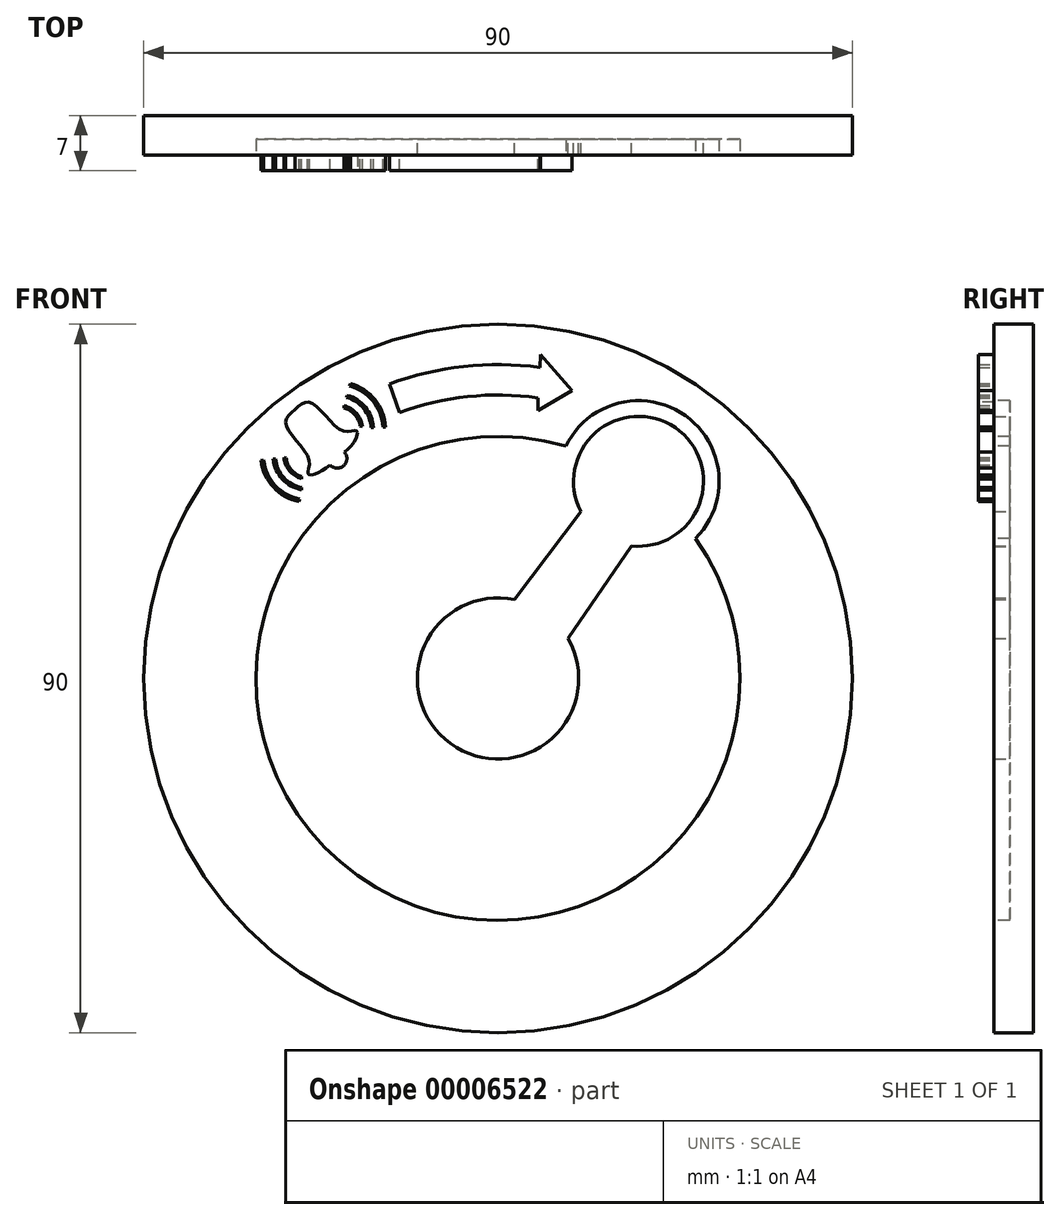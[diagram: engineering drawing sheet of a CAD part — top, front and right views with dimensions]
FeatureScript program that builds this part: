
annotation { "Feature Type Name" : "Feature", "Feature Type Description" : "" }
export const myFeature = defineFeature(function(context is Context, id is Id, definition is map)
    precondition{}
    {
        {
            var Q0;
            Q0=qCreatedBy(makeId("Front.planeOp"),FACE);
            var sketch = newSketch(context, id + "F0", { "sketchPlane" : qUnion([Q0])});
            skCircle(sketch, "E0", {"center": v(0, 0) * mm, "radius": 45 * mm});
            skSolve(sketch);
        }
        {
            var Q0;
            Q0=makeQuery(id+"F0.imprint","IMPRINT",FACE,{"disambiguationData":[TD([[makeQuery(id+"F0.imprint","IMPRINT",EDGE,{"derivedFrom":sQuery(id+"F0.wireOp",EDGE,"E0")}),1.0]])]});
            extrude(context, id + "F1", {"entities" : qUnion([Q0]), "depth" : 5 * mm});
        }
        {
            var Q0;
            Q0=makeQuery(id+"F1.opExtrude","CAP_FACE",FACE,{"disambiguationData":[OSD([sQuery(id+"F0.wireOp",EDGE,"E0")])],"isStart":false});
            var sketch = newSketch(context, id + "F2", { "sketchPlane" : qUnion([Q0])});
            skCircle(sketch, "E1", {"center": v(0, 0) * mm, "radius": 30.75 * mm});
            skCircle(sketch, "E2", {"center": v(17.84, 25.04) * mm, "radius": 10.25 * mm});
            skSolve(sketch);
        }
        {
            var Q0;
            {var subQ0=sQuery(id+"F2.wireOp",EDGE,"E2");var subQ1=sQuery(id+"F2.wireOp",EDGE,"E1");var subQ3=makeQuery(id+"F2.imprint","INTERSECT",VERTEX,{"disambiguationData":[OD(0.0)],"derivedFrom":[subQ1,subQ0]});var subQ5=makeQuery(id+"F2.imprint","IMPRINT",EDGE,{"disambiguationData":[TD([[subQ3,1.0]])],"derivedFrom":subQ1});Q0=qUnion([makeQuery(id+"F2.imprint","IMPRINT",FACE,{"disambiguationData":[TD([[subQ5,1.0]])]}),makeQuery(id+"F2.imprint","IMPRINT",FACE,{"disambiguationData":[TD([[subQ5,-1.0]])]}),makeQuery(id+"F2.imprint","IMPRINT",FACE,{"disambiguationData":[TD([[makeQuery(id+"F2.imprint","IMPRINT",EDGE,{"disambiguationData":[TD([[subQ3,-1.0]])],"derivedFrom":subQ1}),1.0]])]})]);}
            extrude(context, id + "F3", {"entities" : qUnion([Q0]), "operationType" : NewBodyOperationType.REMOVE, "oppositeDirection" : true, "depth" : 2 * mm});
        }
        {
            var Q0;
            Q0=makeQuery(id+"F3.boolean.opBoolean","COPY",FACE,{"derivedFrom":makeQuery(id+"F3.opExtrude","CAP_FACE",FACE,{"disambiguationData":[OSD([sQuery(id+"F2.wireOp",EDGE,"E1"),sQuery(id+"F2.wireOp",EDGE,"E2")])],"isStart":false})});
            var sketch = newSketch(context, id + "F4", { "sketchPlane" : qUnion([Q0])});
            skCircle(sketch, "E3", {"center": v(17.84, 25.04) * mm, "radius": 8.25 * mm});
            skSolve(sketch);
        }
        {
            var Q0;
            Q0=makeQuery(id+"F4.imprint","IMPRINT",FACE,{"disambiguationData":[TD([[makeQuery(id+"F4.imprint","IMPRINT",EDGE,{"derivedFrom":sQuery(id+"F4.wireOp",EDGE,"E3")}),1.0]])]});
            extrude(context, id + "F5", {"entities" : qUnion([Q0]), "operationType" : NewBodyOperationType.ADD, "depth" : 2 * mm});
        }
        {
            var Q0;
            Q0=makeQuery(id+"F3.boolean.opBoolean","COPY",FACE,{"derivedFrom":makeQuery(id+"F3.opExtrude","CAP_FACE",FACE,{"disambiguationData":[OSD([sQuery(id+"F2.wireOp",EDGE,"E1"),sQuery(id+"F2.wireOp",EDGE,"E2")])],"isStart":false})});
            var sketch = newSketch(context, id + "F6", { "sketchPlane" : qUnion([Q0])});
            skCircle(sketch, "E4", {"center": v(0, 0) * mm, "radius": 10.24 * mm});
            skLineSegment(sketch, "E5", {"start": v(2.1, 10.02) * mm, "end": v(10.52, 21.22) * mm});
            skLineSegment(sketch, "E6", {"start": v(8.9, 5.07) * mm, "end": v(16.92, 16.84) * mm});
            skLineSegment(sketch, "E7", {"start": v(10.52, 21.22) * mm, "end": v(16.92, 16.84) * mm});
            skSolve(sketch);
        }
        {
            var Q0;
            {var subQ0=sQuery(id+"F6.wireOp",EDGE,"E4");var subQ3=sQuery(id+"F6.wireOp",EDGE,"E5");var subQ4=makeQuery(id+"F6.imprint","INTERSECT",VERTEX,{"derivedFrom":[subQ0,subQ3]});var subQ5=makeQuery(id+"F6.imprint","IMPRINT",EDGE,{"disambiguationData":[TD([[subQ4,1.0]])],"derivedFrom":subQ0});var subQ7=sQuery(id+"F6.wireOp",EDGE,"E7");Q0=qUnion([makeQuery(id+"F6.imprint","IMPRINT",FACE,{"disambiguationData":[TD([[subQ5,1.0]])]}),makeQuery(id+"F6.imprint","IMPRINT",FACE,{"disambiguationData":[TD([[makeQuery(id+"F6.imprint","IMPRINT",EDGE,{"derivedFrom":subQ3}),-1.0]])]}),makeQuery(id+"F6.imprint","IMPRINT",FACE,{"disambiguationData":[TD([[makeQuery(id+"F6.imprint","IMPRINT",EDGE,{"derivedFrom":subQ7}),-1.0]])]})]);}
            extrude(context, id + "F7", {"entities" : qUnion([Q0]), "operationType" : NewBodyOperationType.ADD, "depth" : 2 * mm});
        }
        {
            var Q0;
            Q0=makeQuery(id+"F1.opExtrude","CAP_FACE",FACE,{"disambiguationData":[OSD([sQuery(id+"F0.wireOp",EDGE,"E0")])],"isStart":false});
            var sketch = newSketch(context, id + "F8", { "sketchPlane" : qUnion([Q0])});
            skArc(sketch, "E8", {"start": v(5.05, 35.65) * mm, "mid": v(-3.85, 35.8) * mm, "end": v(-12.5, 33.76) * mm});
            skArc(sketch, "E9", {"start": v(5.3, 39.5) * mm, "mid": v(-4.37, 39.63) * mm, "end": v(-13.78, 37.41) * mm});
            skLineSegment(sketch, "E10", {"start": v(-13.78, 37.41) * mm, "end": v(-12.5, 33.76) * mm});
            skLineSegment(sketch, "E11", {"start": v(5.05, 35.65) * mm, "end": v(5.05, 34.04) * mm});
            skLineSegment(sketch, "E12", {"start": v(5.05, 34.04) * mm, "end": v(9.4, 36.59) * mm});
            skLineSegment(sketch, "E13", {"start": v(9.4, 36.59) * mm, "end": v(5.39, 41.11) * mm});
            skLineSegment(sketch, "E14", {"start": v(5.39, 41.11) * mm, "end": v(5.3, 39.5) * mm});
            skLineSegment(sketch, "E15", {"start": v(-13.78, 37.41) * mm, "end": v(-13.44, 36.43) * mm});
            skSolve(sketch);
        }
        {
            var Q0;
            Q0=makeQuery(id+"F8.imprint","IMPRINT",FACE,{"disambiguationData":[TD([[makeQuery(id+"F8.imprint","IMPRINT",EDGE,{"derivedFrom":sQuery(id+"F8.wireOp",EDGE,"E8")}),-1.0]])]});
            extrude(context, id + "F9", {"entities" : qUnion([Q0]), "operationType" : NewBodyOperationType.ADD, "depth" : 2 * mm});
        }
        {
            var Q0;
            Q0=makeQuery(id+"F1.opExtrude","CAP_FACE",FACE,{"disambiguationData":[OSD([sQuery(id+"F0.wireOp",EDGE,"E0")])],"isStart":false});
            var sketch = newSketch(context, id + "F10", { "sketchPlane" : qUnion([Q0])});
            skFitSpline(sketch, "E16", {"points": [v(-25.8, 34.15) * mm, v(-23.73, 35) * mm, v(-19.68, 31.43) * mm, v(-17.99, 31.46) * mm, v(-18.08, 30.4) * mm, v(-20.44, 27.94) * mm], "startDerivative": vector(10.59, 9.7) * mm, "endDerivative": vector(-12.74, -9.93) * mm});
            skFitSpline(sketch, "E17.0.MirrorCS", {"points": [v(-25.8, 34.15) * mm, v(-26.94, 32.23) * mm, v(-24, 27.7) * mm, v(-24.15, 26.02) * mm, v(-23.2, 25.97) * mm, v(-20.44, 27.94) * mm], "startDerivative": vector(-11.14, -9.06) * mm, "endDerivative": vector(11.68, 11.16) * mm});
            skCircle(sketch, "E18", {"center": v(-20.44, 27.94) * mm, "radius": 1.24 * mm});
            skArc(sketch, "E19", {"start": v(-25.14, 34.76) * mm, "mid": v(-26.4, 34.85) * mm, "end": v(-26.5, 33.59) * mm});
            skSolve(sketch);
        }
        {
            var Q0;
            Q0 = qSketchRegion(id + "F10", true);
            extrude(context, id + "F11", {"entities" : qUnion([Q0]), "operationType" : NewBodyOperationType.ADD, "depth" : 2 * mm});
        }
        {
            var Q0;
            Q0=makeQuery(id+"F1.opExtrude","CAP_FACE",FACE,{"disambiguationData":[OSD([sQuery(id+"F0.wireOp",EDGE,"E0")])],"isStart":false});
            var sketch = newSketch(context, id + "F12", { "sketchPlane" : qUnion([Q0])});
            skArc(sketch, "E20", {"start": v(-26.93, 28.03) * mm, "mid": v(-26.29, 26.55) * mm, "end": v(-24.95, 25.65) * mm});
            skArc(sketch, "E21", {"start": v(-27.2, 28.06) * mm, "mid": v(-26.48, 26.36) * mm, "end": v(-24.93, 25.36) * mm});
            skArc(sketch, "E22", {"start": v(-28.28, 27.89) * mm, "mid": v(-27.2, 25.53) * mm, "end": v(-24.93, 24.24) * mm});
            skArc(sketch, "E23.0", {"start": v(-28.56, 27.85) * mm, "mid": v(-27.4, 25.33) * mm, "end": v(-25, 23.96) * mm});
            skArc(sketch, "E24.0", {"start": v(-29.76, 27.71) * mm, "mid": v(-28.3, 24.52) * mm, "end": v(-25.23, 22.78) * mm});
            skArc(sketch, "E25.0", {"start": v(-30.1, 27.68) * mm, "mid": v(-28.54, 24.3) * mm, "end": v(-25.3, 22.45) * mm});
            skLineSegment(sketch, "E26", {"start": v(-30.1, 27.68) * mm, "end": v(-29.76, 27.71) * mm});
            skLineSegment(sketch, "E27", {"start": v(-28.56, 27.85) * mm, "end": v(-28.28, 27.89) * mm});
            skLineSegment(sketch, "E28", {"start": v(-27.2, 28.06) * mm, "end": v(-26.93, 28.03) * mm});
            skLineSegment(sketch, "E29", {"start": v(-24.95, 25.65) * mm, "end": v(-24.93, 25.36) * mm});
            skLineSegment(sketch, "E30", {"start": v(-24.93, 24.24) * mm, "end": v(-25, 23.96) * mm});
            skLineSegment(sketch, "E31", {"start": v(-25.23, 22.78) * mm, "end": v(-25.3, 22.45) * mm});
            skLineSegment(sketch, "E32", {"start": v(-25.8, 34.15) * mm, "end": v(-19.63, 27) * mm});
            skLineSegment(sketch, "E33.0.MirrorCS", {"start": v(-19.17, 35.97) * mm, "end": v(-19.24, 35.69) * mm});
            skLineSegment(sketch, "E33.1.MirrorCS", {"start": v(-19.57, 34.65) * mm, "end": v(-19.57, 34.37) * mm});
            skLineSegment(sketch, "E33.2.MirrorCS", {"start": v(-14.64, 31.93) * mm, "end": v(-14.3, 31.95) * mm});
            skLineSegment(sketch, "E33.3.MirrorCS", {"start": v(-18.77, 37.45) * mm, "end": v(-18.85, 37.13) * mm});
            skArc(sketch, "E33.4.MirrorCS", {"start": v(-19.24, 35.69) * mm, "mid": v(-17.06, 34.27) * mm, "end": v(-16.12, 31.85) * mm});
            skArc(sketch, "E33.5.MirrorCS", {"start": v(-18.77, 37.45) * mm, "mid": v(-15.64, 35.42) * mm, "end": v(-14.3, 31.95) * mm});
            skArc(sketch, "E33.6.MirrorCS", {"start": v(-18.85, 37.13) * mm, "mid": v(-15.9, 35.21) * mm, "end": v(-14.64, 31.93) * mm});
            skArc(sketch, "E33.7.MirrorCS", {"start": v(-19.57, 34.65) * mm, "mid": v(-18, 33.69) * mm, "end": v(-17.23, 32.01) * mm});
            skArc(sketch, "E33.8.MirrorCS", {"start": v(-19.57, 34.37) * mm, "mid": v(-18.2, 33.52) * mm, "end": v(-17.51, 32.07) * mm});
            skArc(sketch, "E33.9.MirrorCS", {"start": v(-19.17, 35.97) * mm, "mid": v(-16.84, 34.45) * mm, "end": v(-15.84, 31.86) * mm});
            skLineSegment(sketch, "E34", {"start": v(-17.51, 32.07) * mm, "end": v(-17.23, 32.01) * mm});
            skLineSegment(sketch, "E35", {"start": v(-16.12, 31.85) * mm, "end": v(-15.84, 31.86) * mm});
            skSolve(sketch);
        }
        {
            var Q0;
            {Q0=qUnion([makeQuery(id+"F12.imprint","IMPRINT",FACE,{"disambiguationData":[TD([[makeQuery(id+"F12.imprint","IMPRINT",EDGE,{"derivedFrom":sQuery(id+"F12.wireOp",EDGE,"E20")}),-1.0]])]}),makeQuery(id+"F12.imprint","IMPRINT",FACE,{"disambiguationData":[TD([[makeQuery(id+"F12.imprint","IMPRINT",EDGE,{"derivedFrom":sQuery(id+"F12.wireOp",EDGE,"E22")}),-1.0]])]}),makeQuery(id+"F12.imprint","IMPRINT",FACE,{"disambiguationData":[TD([[makeQuery(id+"F12.imprint","IMPRINT",EDGE,{"derivedFrom":sQuery(id+"F12.wireOp",EDGE,"E24.0")}),-1.0]])]}),makeQuery(id+"F12.imprint","IMPRINT",FACE,{"disambiguationData":[TD([[makeQuery(id+"F12.imprint","IMPRINT",EDGE,{"derivedFrom":sQuery(id+"F12.wireOp",EDGE,"E33.0.MirrorCS")}),1.0]])]}),makeQuery(id+"F12.imprint","IMPRINT",FACE,{"disambiguationData":[TD([[makeQuery(id+"F12.imprint","IMPRINT",EDGE,{"derivedFrom":sQuery(id+"F12.wireOp",EDGE,"E33.1.MirrorCS")}),1.0]])]}),makeQuery(id+"F12.imprint","IMPRINT",FACE,{"disambiguationData":[TD([[makeQuery(id+"F12.imprint","IMPRINT",EDGE,{"derivedFrom":sQuery(id+"F12.wireOp",EDGE,"E33.2.MirrorCS")}),1.0]])]})]);}
            extrude(context, id + "F13", {"entities" : qUnion([Q0]), "operationType" : NewBodyOperationType.ADD, "depth" : 2 * mm});
        }
    });
